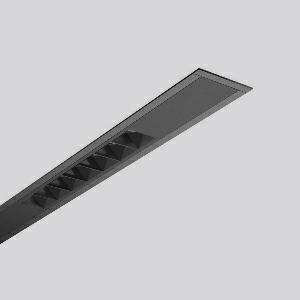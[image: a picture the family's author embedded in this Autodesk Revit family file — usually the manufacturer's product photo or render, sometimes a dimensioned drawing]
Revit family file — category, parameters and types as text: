
# Revit family: less_is_more_beamline_312468_003_1_76_9515
name_source: partatom
category: Lighting Fixtures
units: mm (PartAtom-declared; Revit-internal decimal feet)

## family parameters
Cut with Voids When Loaded = No
Host = Face
Light Source = No
Part Type = Normal
Room Calculation Point = No
Round Connector Dimension = Use Diameter
Shared = No

## types (1)
- LESS IS MORE BEAMLINE (1 x LED Modul 940, 1950 lm, 4000)
    Apparent Load = 48 VA
    CIE Flux Codes = 100 100 100 100 100
    Color Rendering = 92
    Color Temperature = 4000
    Default Elevation = 1800 mm
    Description = Series: LESS IS MORE BEAMLINE
Linear recessed ceiling and wall luminaire for aesthetically sophisticated lighting. Luminaire with two LED light units. Housing: extruded aluminium profile, powder-coated. End cap aluminium powder-coated. LED light unit with MRS technology: Mini-Reflector-System made of metallised thermoplastic with prismatic black glare-suppressing frame for pleasant glare-free light (RUG < 10). Each LED light unit has 7 reflector elements. Narrow beam light distribution. Ceiling installation with pre-assembled SBS mounting system. LED unit with integrated converter interchangeable and removable. Suitable for through-wiring. 
Colour: deep black, matt (RAL 9005)
Length: 1141 mm
Width: 71 mm
Height: 1.5 mm
Cut-out length: 1128 mm
Cut-out width: 60 mm
Recess height: 125 mm
Luminaire: recess height: 106 mm
Lamp: LED
Socket: without socket
Colour temperature: 4000K
Colour rendering index (CRI): 90
System power: 48 W
Rated luminous flux: 3900 lm
Luminous efficiency: 81 lm/W
Control gear: Converter, dimmable, DALI
Protection class: I
Type of protection: IP 20
    Height = 0 mm  [stored 0 ft]
    Lamp = 1 x LED Modul 940
    Lamp Light Flux = 1950 lm
    Lamp count = 1
    Length = 1141 mm
    Lifetime = 50000 h
    Luminous efficacy = 81 lm/W
    Manufacturer = RZB
    ModVariant = No
    Model = 312468.003.1.76
    Mounting Place = Ceiling, Wall
    Mounting Type = Recessed
    Number of Poles = 1
    OnlyDefault = Yes
    Power Factor = 1
    Product Name = LESS IS MORE BEAMLINE
    Product group = Recessed LED linear luminaires
    ProductGroupID = 407
    Protection Class = Protection class I
    Protection Degree = IP 20
    RLX_Detail_Level = 1
    RLX_Emergency_Light_Flux = 0 lm
    RLX_Emergency_Type = 0
    RLX_Emergency_Type_DB = No
    RlxData = <blob elided: 23961 chars, md5=6878fedd>
    Socket = socket
    Standby Power = 0 W
    System Light Flux = 3900 lm
    System Power = 48 W
    Type Comments = Product without accessories
    Type Image = 312465.003.jpg
    URL = http://relux.com
    VarID = ---
    Voltage = 230 V
    Voltage Range = 220-240 V
    Weight = 0.00 kg
    Width = 71 mm

note: [stored X ft] marks values corroborated as IEEE doubles in the binary element streams (Revit-internal decimal feet)

## geometry (parser evidence)
native form markers: Blend x4, Sweep x15
no freeform markers — native parametric forms only
